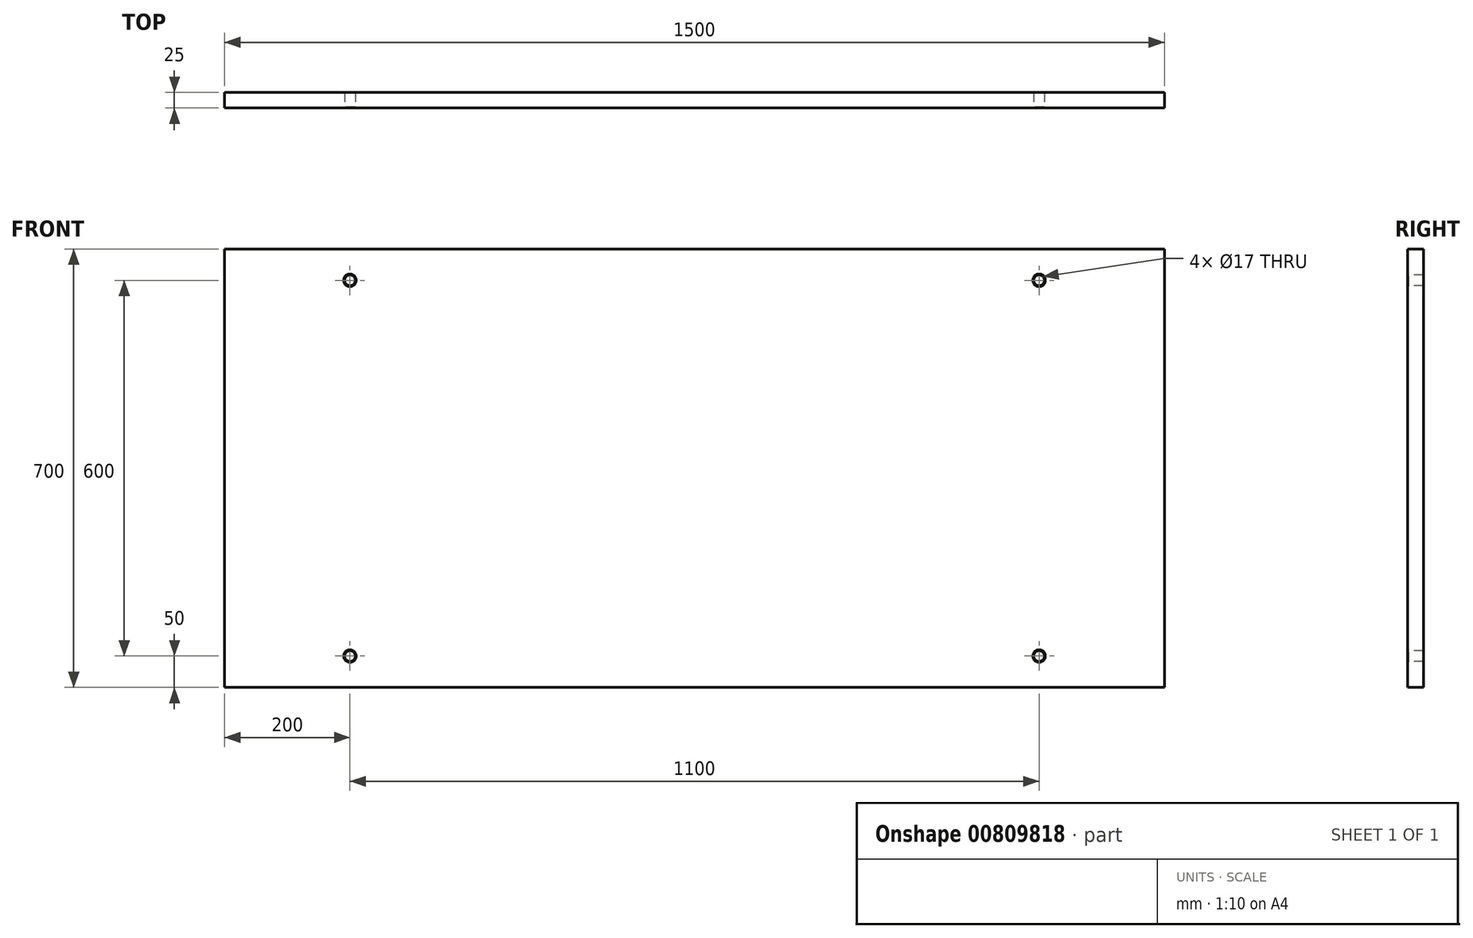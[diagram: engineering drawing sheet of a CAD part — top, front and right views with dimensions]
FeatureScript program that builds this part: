
annotation { "Feature Type Name" : "Feature", "Feature Type Description" : "" }
export const myFeature = defineFeature(function(context is Context, id is Id, definition is map)
    precondition{}
    {
        {
            var Q0;
            Q0=qCreatedBy(makeId("Front.planeOp"),FACE);
            var sketch = newSketch(context, id + "F0", { "sketchPlane" : qUnion([Q0])});
            skLineSegment(sketch, "E0.bottom", {"start": v(-750, 350) * mm, "end": v(750, 350) * mm});
            skLineSegment(sketch, "E0.top", {"start": v(-750, -350) * mm, "end": v(750, -350) * mm});
            skLineSegment(sketch, "E0.left", {"start": v(-750, 350) * mm, "end": v(-750, -350) * mm});
            skLineSegment(sketch, "E0.right", {"start": v(750, 350) * mm, "end": v(750, -350) * mm});
            skSolve(sketch);
        }
        {
            var Q0;
            Q0=makeQuery(id+"F0.imprint","IMPRINT",FACE,{"disambiguationData":[TD([[makeQuery(id+"F0.imprint","IMPRINT",EDGE,{"derivedFrom":sQuery(id+"F0.wireOp",EDGE,"E0.bottom")}),-1.0]])]});
            extrude(context, id + "F1", {"entities" : qUnion([Q0]), "depth" : 25 * mm, "offsetDistance" : 25 * mm});
        }
        {
            var Q0;
            Q0=makeQuery(id+"F1.opExtrude","CAP_FACE",FACE,{"disambiguationData":[OSD([sQuery(id+"F0.wireOp",EDGE,"E0.bottom"),sQuery(id+"F0.wireOp",EDGE,"E0.top"),sQuery(id+"F0.wireOp",EDGE,"E0.left"),sQuery(id+"F0.wireOp",EDGE,"E0.right")])],"isStart":false});
            var sketch = newSketch(context, id + "F2", { "sketchPlane" : qUnion([Q0])});
            skPoint(sketch, "E1", {"position": v(-550, 300) * mm});
            skPoint(sketch, "E2", {"position": v(-550, -300) * mm});
            skPoint(sketch, "E3", {"position": v(550, 300) * mm});
            skPoint(sketch, "E4", {"position": v(550, -300) * mm});
            skSolve(sketch);
        }
        {
            var Q0;
            Q0=sQuery(id+"F2.wireOp",VERTEX,"E1");
            var Q1;
            Q1=sQuery(id+"F2.wireOp",VERTEX,"E3");
            var Q2;
            Q2=sQuery(id+"F2.wireOp",VERTEX,"E4");
            var Q3;
            Q3=sQuery(id+"F2.wireOp",VERTEX,"E2");
            var Q4;
            Q4=makeQuery(id+"F1.opExtrude","SWEPT_BODY",BODY,{"disambiguationData":[OSD([sQuery(id+"F0.wireOp",EDGE,"E0.bottom"),sQuery(id+"F0.wireOp",EDGE,"E0.top"),sQuery(id+"F0.wireOp",EDGE,"E0.left"),sQuery(id+"F0.wireOp",EDGE,"E0.right")])]});
            hole(context, id + "F3", {"style" : HoleStyle.C_SINK, "endStyle" : HoleEndStyle.THROUGH, "holeDiameter" : 17 * mm, "cSinkDiameter" : 20 * mm, "cSinkAngle" : 90 * degree, "majorDiameter" : 5 * mm, "isTappedThrough" : true, "tappedDepth" : 12 * mm, "tapClearance" : 3, "locations" : qUnion([Q0, Q1, Q2, Q3]), "scope" : qUnion([Q4])});
        }
    });
